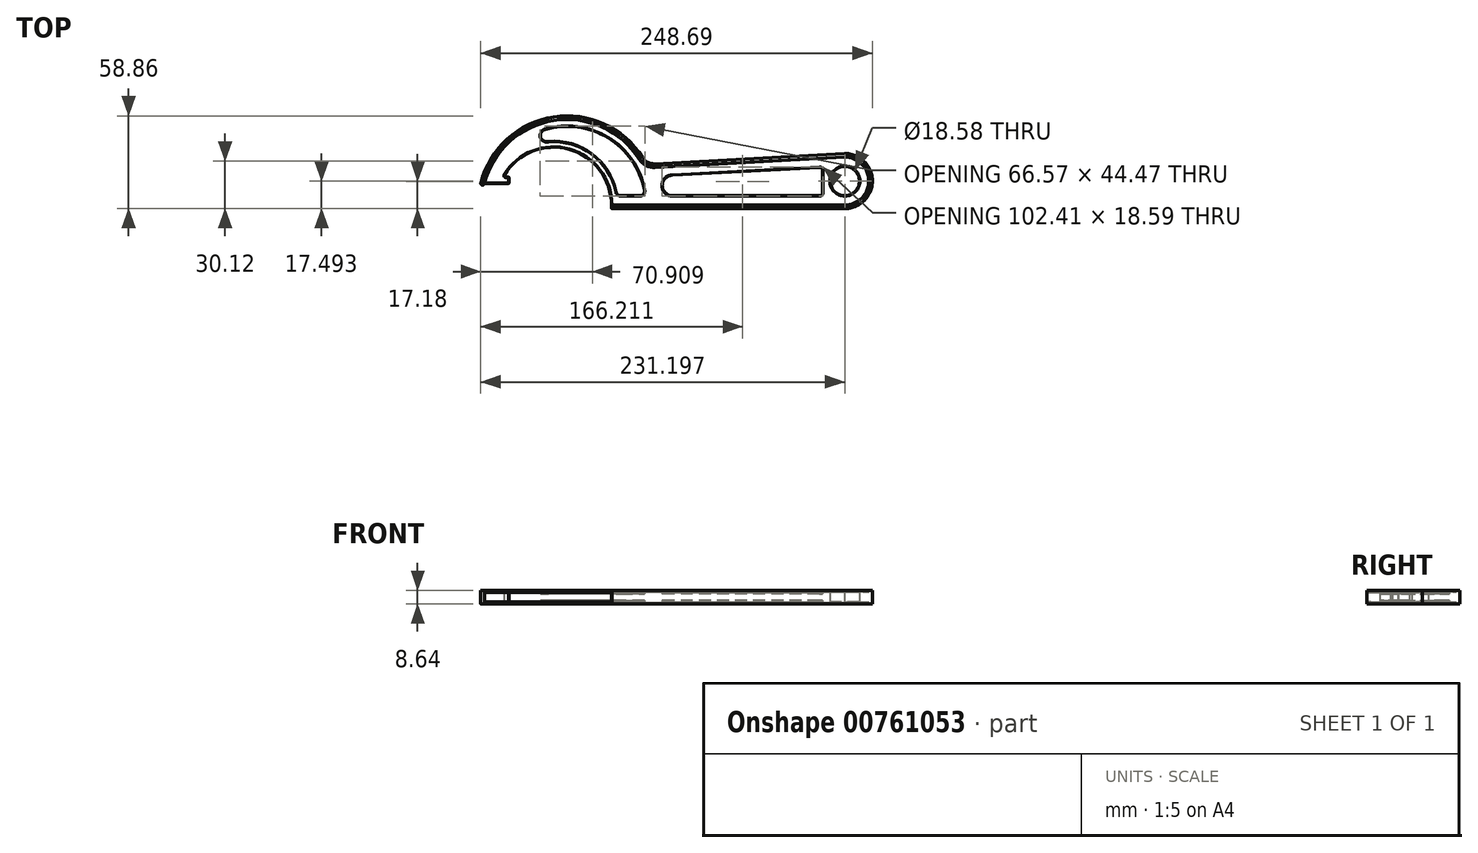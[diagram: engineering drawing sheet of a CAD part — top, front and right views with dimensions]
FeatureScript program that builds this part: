
annotation { "Feature Type Name" : "Feature", "Feature Type Description" : "" }
export const myFeature = defineFeature(function(context is Context, id is Id, definition is map)
    precondition{}
    {
        {
            var Q0;
            Q0=qCreatedBy(makeId("Top.planeOp"),FACE);
            var sketch = newSketch(context, id + "F0", { "sketchPlane" : qUnion([Q0])});
            skArc(sketch, "E0", {"start": v(-24.07, 0) * mm, "mid": v(-50.83, 35.31) * mm, "end": v(-92.06, 19.1) * mm});
            skArc(sketch, "E1", {"start": v(-6.45, 29.1) * mm, "mid": v(-60.76, 53.62) * mm, "end": v(-104.85, 13.54) * mm});
            skLineSegment(sketch, "E2", {"start": v(-24.07, 0) * mm, "end": v(124.1, 0) * mm});
            skLineSegment(sketch, "E3", {"start": v(3.68, 23.88) * mm, "end": v(124.1, 30.4) * mm});
            skArc(sketch, "E4", {"start": v(124.1, 0) * mm, "mid": v(139.3, 15.2) * mm, "end": v(124.1, 30.4) * mm});
            skCircle(sketch, "E5", {"center": v(124.1, 15.2) * mm, "radius": 9.29 * mm});
            skLineSegment(sketch, "E6", {"start": v(-104.85, 13.54) * mm, "end": v(-89.1, 13.54) * mm});
            skLineSegment(sketch, "E7", {"start": v(-89.1, 13.54) * mm, "end": v(-89.1, 17.74) * mm});
            skLineSegment(sketch, "E8", {"start": v(-89.1, 17.74) * mm, "end": v(-91.3, 17.74) * mm});
            skArc(sketch, "E9.0", {"start": v(-4.38, 30.1) * mm, "mid": v(-60.98, 55.9) * mm, "end": v(-107.06, 14.1) * mm});
            skLineSegment(sketch, "E9.1", {"start": v(3.25, 26.15) * mm, "end": v(124.03, 32.7) * mm});
            skArc(sketch, "E9.2", {"start": v(124.1, -2.29) * mm, "mid": v(141.59, 15.24) * mm, "end": v(124.03, 32.7) * mm});
            skLineSegment(sketch, "E9.3", {"start": v(-24.07, -2.29) * mm, "end": v(124.1, -2.29) * mm});
            skLineSegment(sketch, "E10", {"start": v(-24.07, 0) * mm, "end": v(-24.07, -2.29) * mm});
            skPoint(sketch, "E11.visualSharp", {"position": v(-1.97, 25.87) * mm});
            skArc(sketch, "E11.filletArc", {"start": v(-4.38, 30.1) * mm, "mid": v(-1.1, 27.08) * mm, "end": v(3.25, 26.15) * mm});
            skPoint(sketch, "E12.visualSharp", {"position": v(-3.35, 23.5) * mm});
            skArc(sketch, "E12.filletArc", {"start": v(-6.45, 29.1) * mm, "mid": v(-2.1, 25.12) * mm, "end": v(3.68, 23.88) * mm});
            skPoint(sketch, "E13.visualSharp", {"position": v(-92.85, 17.74) * mm});
            skArc(sketch, "E13.filletArc", {"start": v(-92.06, 19.1) * mm, "mid": v(-92.08, 18.2) * mm, "end": v(-91.3, 17.74) * mm});
            skLineSegment(sketch, "E14.0", {"start": v(14.68, 18.88) * mm, "end": v(107.92, 23.93) * mm});
            skLineSegment(sketch, "E15", {"start": v(110.06, 21.9) * mm, "end": v(110.06, 7.88) * mm});
            skPoint(sketch, "E16.visualSharp", {"position": v(110.06, 24.05) * mm});
            skArc(sketch, "E16.filletArc", {"start": v(110.06, 21.9) * mm, "mid": v(109.43, 23.38) * mm, "end": v(107.92, 23.93) * mm});
            skPoint(sketch, "E17.visualSharp", {"position": v(110.06, 5.33) * mm});
            skArc(sketch, "E17.filletArc", {"start": v(108.03, 5.85) * mm, "mid": v(109.47, 6.44) * mm, "end": v(110.06, 7.88) * mm});
            skArc(sketch, "E18", {"start": v(14.68, 18.88) * mm, "mid": v(8.16, 12.36) * mm, "end": v(14.68, 5.85) * mm});
            skArc(sketch, "E19.0", {"start": v(-21.11, 8.26) * mm, "mid": v(-36.56, 32.47) * mm, "end": v(-64.17, 40.34) * mm});
            skArc(sketch, "E20.0", {"start": v(-10.1, 26.79) * mm, "mid": v(-34.72, 46.78) * mm, "end": v(-66.4, 47.93) * mm});
            skPoint(sketch, "E21.third.point", {"position": v(-49.93, 49.91) * mm});
            skLineSegment(sketch, "E22", {"start": v(-6.19, 5.85) * mm, "end": v(-18.15, 5.85) * mm});
            skArc(sketch, "E23.trimOffspring", {"start": v(-3.21, 9.45) * mm, "mid": v(-26.3, 42.68) * mm, "end": v(-66.4, 47.93) * mm});
            skLineSegment(sketch, "E24", {"start": v(14.68, 5.85) * mm, "end": v(108.03, 5.85) * mm});
            skPoint(sketch, "E25.visualSharp", {"position": v(-20.68, 5.85) * mm});
            skArc(sketch, "E25.filletArc", {"start": v(-21.11, 8.26) * mm, "mid": v(-20.06, 6.53) * mm, "end": v(-18.15, 5.85) * mm});
            skPoint(sketch, "E26.visualSharp", {"position": v(-2.66, 5.85) * mm});
            skArc(sketch, "E26.filletArc", {"start": v(-6.19, 5.85) * mm, "mid": v(-3.85, 6.95) * mm, "end": v(-3.21, 9.45) * mm});
            skArc(sketch, "E27", {"start": v(-66.4, 47.93) * mm, "mid": v(-69.08, 43.02) * mm, "end": v(-64.17, 40.34) * mm});
            skArc(sketch, "E28", {"start": v(-107.06, 14.1) * mm, "mid": v(-106.24, 12.71) * mm, "end": v(-104.85, 13.54) * mm});
            skSolve(sketch);
        }
        {
            var Q0;
            Q0=makeQuery(id+"F0.imprint","IMPRINT",FACE,{"disambiguationData":[TD([[makeQuery(id+"F0.imprint","IMPRINT",EDGE,{"derivedFrom":sQuery(id+"F0.wireOp",EDGE,"E0")}),-1.0]])]});
            var Q1;
            Q1=makeQuery(id+"F0.imprint","IMPRINT",FACE,{"disambiguationData":[TD([[makeQuery(id+"F0.imprint","IMPRINT",EDGE,{"derivedFrom":sQuery(id+"F0.wireOp",EDGE,"E19.0")}),-1.0]])]});
            var Q2;
            Q2=makeQuery(id+"F0.imprint","IMPRINT",FACE,{"disambiguationData":[TD([[makeQuery(id+"F0.imprint","IMPRINT",EDGE,{"derivedFrom":sQuery(id+"F0.wireOp",EDGE,"E14.0")}),-1.0]])]});
            extrude(context, id + "F1", {"entities" : qUnion([Q0, Q1, Q2]), "endBound" : BoundingType.SYMMETRIC, "depth" : 4.06 * mm, "offsetDistance" : 25.4 * mm});
        }
        {
            var Q0;
            Q0=makeQuery(id+"F0.imprint","IMPRINT",FACE,{"disambiguationData":[TD([[makeQuery(id+"F0.imprint","IMPRINT",EDGE,{"derivedFrom":sQuery(id+"F0.wireOp",EDGE,"E0")}),-1.0]])]});
            extrude(context, id + "F2", {"entities" : qUnion([Q0]), "operationType" : NewBodyOperationType.ADD, "endBound" : BoundingType.SYMMETRIC, "depth" : 6.6 * mm, "offsetDistance" : 25.4 * mm});
        }
        {
            var Q0;
            Q0=makeQuery(id+"F0.imprint","IMPRINT",FACE,{"disambiguationData":[TD([[makeQuery(id+"F0.imprint","IMPRINT",EDGE,{"derivedFrom":sQuery(id+"F0.wireOp",EDGE,"E1")}),-1.0]])]});
            extrude(context, id + "F3", {"entities" : qUnion([Q0]), "operationType" : NewBodyOperationType.ADD, "endBound" : BoundingType.SYMMETRIC, "depth" : 8.64 * mm, "offsetDistance" : 25.4 * mm});
        }
        {
            var Q0;
            {var subQ0=sQuery(id+"F0.wireOp",EDGE,"E8");var subQ1=sQuery(id+"F0.wireOp",EDGE,"E7");Q0=makeQuery(id+"F2.boolean.opBoolean","MERGE",EDGE,{"derivedFrom":[makeQuery(id+"F1.opExtrude","SWEPT_EDGE",EDGE,{"disambiguationData":[OSD([subQ1,subQ0])]}),makeQuery(id+"F2.opExtrude","SWEPT_EDGE",EDGE,{"disambiguationData":[OSD([subQ1,subQ0])]})]});}
            var Q1;
            {var subQ0=sQuery(id+"F0.wireOp",EDGE,"E7");var subQ1=sQuery(id+"F0.wireOp",EDGE,"E6");Q1=makeQuery(id+"F2.boolean.opBoolean","MERGE",EDGE,{"derivedFrom":[makeQuery(id+"F1.opExtrude","SWEPT_EDGE",EDGE,{"disambiguationData":[OSD([subQ1,subQ0])]}),makeQuery(id+"F2.opExtrude","SWEPT_EDGE",EDGE,{"disambiguationData":[OSD([subQ1,subQ0])]})]});}
            var Q2;
            Q2=makeQuery(id+"F2.opExtrude","CAP_EDGE",EDGE,{"disambiguationData":[OSD([sQuery(id+"F0.wireOp",EDGE,"E0")])],"isStart":false});
            var Q3;
            Q3=makeQuery(id+"F2.opExtrude","CAP_EDGE",EDGE,{"disambiguationData":[OSD([sQuery(id+"F0.wireOp",EDGE,"E0")])],"isStart":true});
            var Q4;
            {var subQ0=sQuery(id+"F0.wireOp",EDGE,"E7");Q4=makeQuery(id+"F2.boolean.opBoolean","MERGE",FACE,{"derivedFrom":[makeQuery(id+"F1.opExtrude","SWEPT_FACE",FACE,{"disambiguationData":[OSD([subQ0])]}),makeQuery(id+"F2.opExtrude","SWEPT_FACE",FACE,{"disambiguationData":[OSD([subQ0])]})]});}
            var Q5;
            Q5=makeQuery(id+"F2.opExtrude","CAP_EDGE",EDGE,{"disambiguationData":[OSD([sQuery(id+"F0.wireOp",EDGE,"E6")])],"isStart":false});
            var Q6;
            Q6=makeQuery(id+"F2.opExtrude","CAP_EDGE",EDGE,{"disambiguationData":[OSD([sQuery(id+"F0.wireOp",EDGE,"E6")])],"isStart":true});
            var Q7;
            Q7=makeQuery(id+"F3.opExtrude","SWEPT_EDGE",EDGE,{"disambiguationData":[OSD([sQuery(id+"F0.wireOp",EDGE,"E9.3"),sQuery(id+"F0.wireOp",EDGE,"E10")])]});
            var Q8;
            {var subQ0=sQuery(id+"F0.wireOp",EDGE,"E5");Q8=makeQuery(id+"F2.boolean.opBoolean","MERGE",FACE,{"derivedFrom":[makeQuery(id+"F1.opExtrude","SWEPT_FACE",FACE,{"disambiguationData":[OSD([subQ0])]}),makeQuery(id+"F2.opExtrude","SWEPT_FACE",FACE,{"disambiguationData":[OSD([subQ0])]})]});}
            var Q9;
            Q9=makeQuery(id+"F2.opExtrude","CAP_EDGE",EDGE,{"disambiguationData":[OSD([sQuery(id+"F0.wireOp",EDGE,"E18")])],"isStart":true});
            var Q10;
            Q10=makeQuery(id+"F2.opExtrude","CAP_EDGE",EDGE,{"disambiguationData":[OSD([sQuery(id+"F0.wireOp",EDGE,"E25.filletArc")])],"isStart":true});
            var Q11;
            Q11=makeQuery(id+"F2.opExtrude","CAP_EDGE",EDGE,{"disambiguationData":[OSD([sQuery(id+"F0.wireOp",EDGE,"E26.filletArc")])],"isStart":false});
            var Q12;
            Q12=makeQuery(id+"F2.opExtrude","CAP_EDGE",EDGE,{"disambiguationData":[OSD([sQuery(id+"F0.wireOp",EDGE,"E18")])],"isStart":false});
            chamfer(context, id + "F4", {"entities" : qUnion([Q0, Q1, Q2, Q3, Q4, Q5, Q6, Q7, Q8, Q9, Q10, Q11, Q12]), "width" : 0.25 * mm, "tangentPropagation" : true});
        }
        {
            var Q0;
            Q0=makeQuery(id+"F3.opExtrude","CAP_FACE",FACE,{"disambiguationData":[OSD([sQuery(id+"F0.wireOp",EDGE,"E1"),sQuery(id+"F0.wireOp",EDGE,"E2"),sQuery(id+"F0.wireOp",EDGE,"E3"),sQuery(id+"F0.wireOp",EDGE,"E4"),sQuery(id+"F0.wireOp",EDGE,"E9.0"),sQuery(id+"F0.wireOp",EDGE,"E9.1"),sQuery(id+"F0.wireOp",EDGE,"E9.2"),sQuery(id+"F0.wireOp",EDGE,"E9.3"),sQuery(id+"F0.wireOp",EDGE,"E10"),sQuery(id+"F0.wireOp",EDGE,"E11.filletArc"),sQuery(id+"F0.wireOp",EDGE,"E12.filletArc"),sQuery(id+"F0.wireOp",EDGE,"E28")])],"isStart":false});
            var Q1;
            Q1=makeQuery(id+"F3.opExtrude","CAP_FACE",FACE,{"disambiguationData":[OSD([sQuery(id+"F0.wireOp",EDGE,"E1"),sQuery(id+"F0.wireOp",EDGE,"E2"),sQuery(id+"F0.wireOp",EDGE,"E3"),sQuery(id+"F0.wireOp",EDGE,"E4"),sQuery(id+"F0.wireOp",EDGE,"E9.0"),sQuery(id+"F0.wireOp",EDGE,"E9.1"),sQuery(id+"F0.wireOp",EDGE,"E9.2"),sQuery(id+"F0.wireOp",EDGE,"E9.3"),sQuery(id+"F0.wireOp",EDGE,"E10"),sQuery(id+"F0.wireOp",EDGE,"E11.filletArc"),sQuery(id+"F0.wireOp",EDGE,"E12.filletArc"),sQuery(id+"F0.wireOp",EDGE,"E28")])],"isStart":true});
            chamfer(context, id + "F5", {"entities" : qUnion([Q0, Q1]), "width" : 0.15 * mm, "tangentPropagation" : true});
        }
    });
